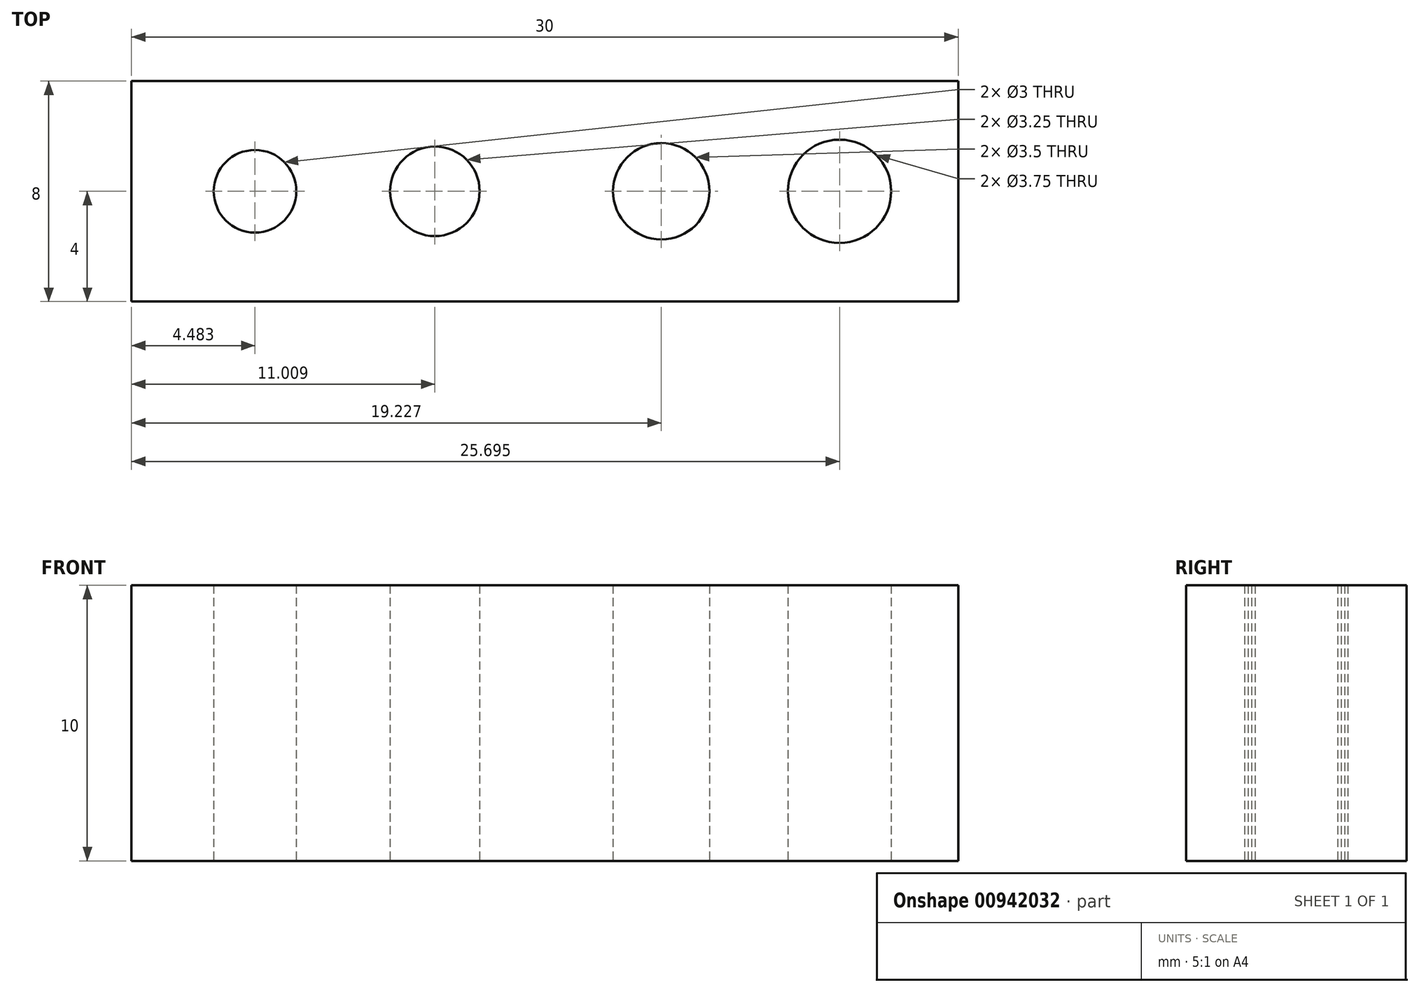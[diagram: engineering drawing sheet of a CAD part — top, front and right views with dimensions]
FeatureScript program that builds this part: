
annotation { "Feature Type Name" : "Feature", "Feature Type Description" : "" }
export const myFeature = defineFeature(function(context is Context, id is Id, definition is map)
    precondition{}
    {
        {
            var Q0;
            Q0=qCreatedBy(makeId("Top.planeOp"),FACE);
            var sketch = newSketch(context, id + "F0", { "sketchPlane" : qUnion([Q0])});
            skLineSegment(sketch, "E0.bottom", {"start": v(15, -4) * mm, "end": v(-15, -4) * mm});
            skLineSegment(sketch, "E0.top", {"start": v(15, 4) * mm, "end": v(-15, 4) * mm});
            skLineSegment(sketch, "E0.left", {"start": v(15, -4) * mm, "end": v(15, 4) * mm});
            skLineSegment(sketch, "E0.right", {"start": v(-15, -4) * mm, "end": v(-15, 4) * mm});
            skPoint(sketch, "E0.middle", {"position": v(0, 0) * mm});
            skCircle(sketch, "E1", {"center": v(-10.52, 0) * mm, "radius": 1.5 * mm});
            skCircle(sketch, "E2", {"center": v(-4, 0) * mm, "radius": 1.63 * mm});
            skCircle(sketch, "E3", {"center": v(4.23, 0) * mm, "radius": 1.75 * mm});
            skCircle(sketch, "E4", {"center": v(10.7, 0) * mm, "radius": 1.88 * mm});
            skSolve(sketch);
        }
        {
            var Q0;
            Q0=makeQuery(id+"F0.imprint","IMPRINT",FACE,{"disambiguationData":[TD([[makeQuery(id+"F0.imprint","IMPRINT",EDGE,{"derivedFrom":sQuery(id+"F0.wireOp",EDGE,"E0.bottom")}),-1.0]])]});
            extrude(context, id + "F1", {"entities" : qUnion([Q0]), "depth" : 10 * mm, "offsetDistance" : 25 * mm});
        }
    });
